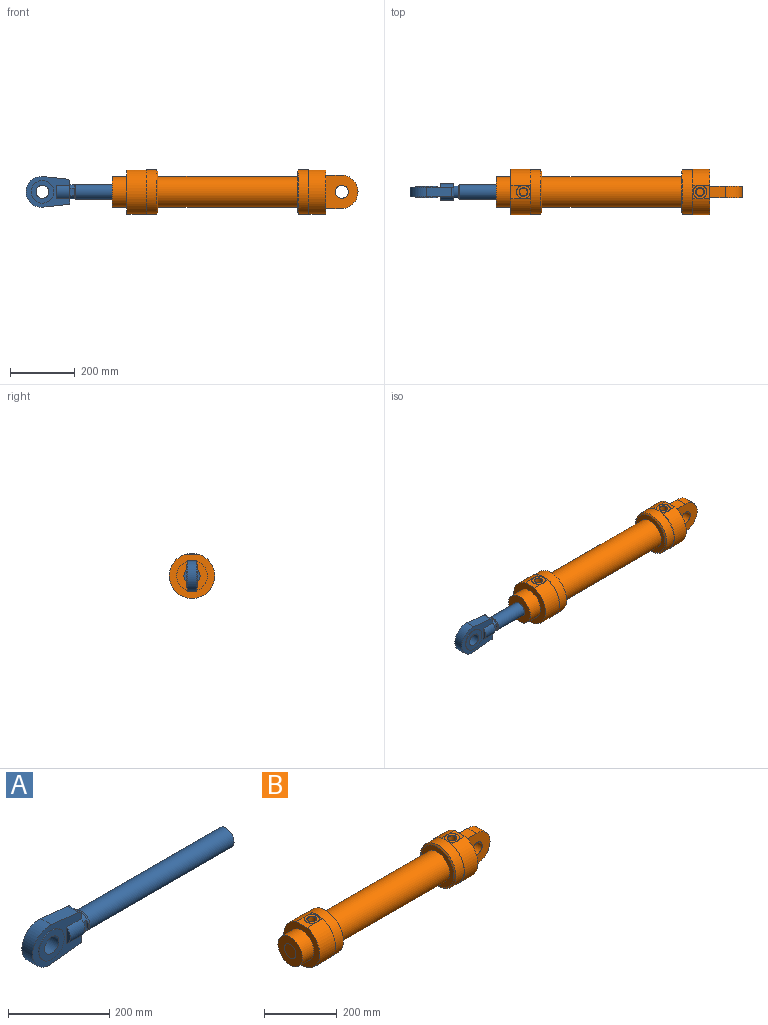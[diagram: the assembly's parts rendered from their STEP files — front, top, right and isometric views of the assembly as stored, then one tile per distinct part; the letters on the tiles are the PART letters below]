
ASSEMBLY  parts=2 mates=1
PART A: 45 faces, bbox 556x50x95 mm
  f0: cylinder r=20mm len=40mm, axis (0,-1,0), area 4398.2mm2, adj f1,f2
  f1: plane 70x70mm, normal (0,1,0), area 2591.8mm2, adj f0,f3
  f2: plane 70x70mm, normal (0,-1,0), area 2591.8mm2, adj f0,f5
  f3: cylinder r=35mm len=70mm, axis (0,-1,0), area 549.8mm2, adj f1,f12
  f4: plane 40x10mm, normal (-1,0,0), area 279.6mm2, adj f11,f12
  f5: cylinder r=35mm len=70mm, axis (0,-1,0), area 549.8mm2, adj f2,f15
  f6: plane 40x10mm, normal (-1,0,0), area 279.6mm2, adj f14,f15
  f7: plane 79.97x30mm, normal (0.1,0,-0.99), area 2412.3mm2, adj f8,f12,f13,f15
  f8: cylinder r=47.5mm len=95mm, axis (0,-1,0), area 4773.9mm2, adj f7,f9,f12,f15
  f9: plane 75.49x30mm, normal (0.1,0,0.99), area 2277.2mm2, adj f8,f10,f12,f15
  f10: cylinder r=9mm len=30mm, axis (0,-1,0), area 396mm2, adj f9,f12,f15,f16
  f11: cylinder r=25mm len=41mm, axis (1,0,0), area 1901mm2, adj f4,f12,f16
  f12: plane 136x95mm, normal (0,1,0), area 5672.5mm2, adj f3,f4,f7,f8,f9,f10,f11,f13
  f13: cylinder r=4mm len=30mm, axis (0,-1,0), area 176mm2, adj f7,f12,f15,f16
  f14: cylinder r=25mm len=41mm, axis (1,0,0), area 1901mm2, adj f6,f15,f16
  f15: plane 136x95mm, normal (0,-1,0), area 5672.5mm2, adj f5,f6,f7,f8,f9,f10,f13,f14
  f16: plane 65.29x50mm, normal (1,0,0), area 1178.1mm2, adj f10,f11,f12,f13,f14,f15,f17,f18
  f17: cone r=21.49mm half-angle=45deg, axis (1,0,0), area 0.6mm2, adj f16,f18,f19,f22
  f18: plane 23.52x13mm, normal (0,-1,0), area 305.7mm2, adj f16,f17,f20,f21,f22,f24
  f19: plane 23.52x13mm, normal (0,1,0), area 305.7mm2, adj f16,f17,f20,f22,f23,f24
  f20: cone r=21.49mm half-angle=45deg, axis (1,0,0), area 0.6mm2, adj f16,f18,f19,f24
  f21: plane 23.52x3.5mm, normal (-1,0,0), area 55.8mm2, adj f18,f25
  f22: cylinder r=21.5mm len=36mm, axis (1,0,0), area 554.2mm2, adj f17,f18,f19,f25
  f23: plane 23.52x3.5mm, normal (-1,0,0), area 55.8mm2, adj f19,f25
  f24: cylinder r=21.5mm len=36mm, axis (1,0,0), area 554.2mm2, adj f18,f19,f20,f25
  f25: cone r=22mm half-angle=15deg, axis (1,0,0), area 534.1mm2, adj f21,f22,f23,f24,f26
  f26: cylinder r=22.5mm len=403.27mm, axis (1,0,0), area 57010.7mm2, adj f25,f27
  f27: plane 45x45mm, normal (1,0,0), area 1590.4mm2, adj f26
  f28: plane 65x65mm, normal (0,1,0), area 299.2mm2, adj f30,f31
  f29: plane 65x65mm, normal (0,-1,0), area 299.2mm2, adj f30,f31
  f30: cylinder r=32.5mm len=65mm, axis (0,-1,0), area 439mm2, adj f28,f29
  f31: cylinder r=31mm len=62mm, axis (0,-1,0), area 418.8mm2, adj f28,f29
  f32: cylinder r=32.5mm len=65mm, axis (0,-1,0), area 439mm2, adj f33,f34
  f33: plane 65x65mm, normal (0,-1,0), area 299.2mm2, adj f32,f35
  f34: plane 65x65mm, normal (0,1,0), area 299.2mm2, adj f32,f35
  f35: cylinder r=31mm len=62mm, axis (0,-1,0), area 418.8mm2, adj f33,f34
  f36: plane 33.16x33.16mm, normal (1,0,0), area 23.8mm2, adj f38,f40
  f37: plane 33.38x33.38mm, normal (-1,0,0), area 35.1mm2, adj f39,f40
  f38: cone r=16.58mm half-angle=45deg, axis (-1,0,0), area 16mm2, adj f36,f39
  f39: cylinder r=16.69mm len=33.38mm, axis (-1,0,0), area 346.9mm2, adj f37,f38
  f40: cylinder r=16.35mm len=32.7mm, axis (1,0,0), area 328.7mm2, adj f36,f37
  f41: plane 33.16x33.16mm, normal (-1,0,0), area 863.6mm2, adj f42
  f42: cone r=16.58mm half-angle=45deg, axis (1,0,0), area 16mm2, adj f41,f44
  f43: plane 33.38x33.38mm, normal (1,0,0), area 874.9mm2, adj f44
  f44: cylinder r=16.69mm len=33.38mm, axis (-1,0,0), area 116.2mm2, adj f42,f43
PART B: 46 faces, bbox 760x140x139 mm
  f0: cylinder r=70mm len=140mm, axis (1,0,0), area 20723.4mm2, adj f1,f14,f21,f29,f34
  f1: cylinder r=21mm len=42mm, axis (0,0,-1), area 62.7mm2, adj f0,f21,f29,f36
  f2: cylinder r=12.12mm len=24.25mm, axis (0,0,-1), area 1502.7mm2, adj f5,f26
  f3: plane 104x100mm, normal (0,1,0), area 7982.8mm2, adj f14,f17,f18,f28,f32
  f4: cone r=13.4mm half-angle=45deg, axis (0,0,1), area 144.6mm2, adj f22,f36
  f5: plane 24.25x24.25mm, normal (0,0,1), area 461.9mm2, adj f2
  f6: cylinder r=47.5mm len=432mm, axis (1,0,0), area 128931mm2, adj f11,f15
  f7: cylinder r=21mm len=42mm, axis (0,0,-1), area 63.1mm2, adj f25,f27,f30,f31
  f8: plane 140x137mm, normal (-1,0,0), area 8224.1mm2, adj f27,f31,f35
  f9: cylinder r=69mm len=138mm, axis (-1,0,0), area 13922.4mm2, adj f10,f24,f34
  f10: cone r=64mm half-angle=60deg, axis (1,0,0), area 2412.4mm2, adj f9,f11
  f11: plane 128x128mm, normal (-1,0,0), area 5779.7mm2, adj f6,f10
  f12: plane 95x95mm, normal (-1,0,0), area 5497.8mm2, adj f35,f37
  f13: plane 32.99x2mm, normal (-1,0,0), area 44.1mm2, adj f23,f30
  f14: plane 140x137mm, normal (1,0,0), area 11672.4mm2, adj f0,f3,f18,f19,f21,f28
  f15: plane 128x128mm, normal (1,0,0), area 5779.7mm2, adj f6,f33
  f16: plane 140x137mm, normal (1,0,0), area 399.3mm2, adj f23,f30,f31
  f17: cylinder r=20mm len=40mm, axis (0,-1,0), area 4398.2mm2, adj f3,f19
  f18: plane 48x35mm, normal (0,0,1), area 1680mm2, adj f3,f14,f19,f32
  f19: plane 104x100mm, normal (0,-1,0), area 7982.8mm2, adj f14,f17,f18,f28,f32
  f20: plane 24.25x24.25mm, normal (0,0,1), area 461.9mm2, adj f22
  f21: plane 40.55x24.52mm, normal (0,0,1), area 529mm2, adj f0,f1,f14
  f22: cylinder r=12.12mm len=24.25mm, axis (0,0,-1), area 1502.7mm2, adj f4,f20
  f23: cylinder r=69mm len=138mm, axis (1,0,0), area 13922.4mm2, adj f13,f16,f33
  f24: plane 32.99x2mm, normal (1,0,0), area 44.1mm2, adj f9,f29
  f25: plane 42x42mm, normal (0,0,1), area 821.3mm2, adj f7,f26
  f26: cone r=13.4mm half-angle=45deg, axis (0,0,1), area 144.6mm2, adj f2,f25
  f27: plane 40.55x33.52mm, normal (0,0,1), area 893.9mm2, adj f7,f8,f31
  f28: plane 48x35mm, normal (0,0,-1), area 1680mm2, adj f3,f14,f19,f32
  f29: plane 40.55x16.52mm, normal (0,0,1), area 204.6mm2, adj f0,f1,f24,f34
  f30: plane 40.55x16.52mm, normal (0,0,1), area 204.6mm2, adj f7,f13,f16,f31
  f31: cylinder r=70mm len=140mm, axis (1,0,0), area 24310.2mm2, adj f7,f8,f16,f27,f30
  f32: cylinder r=52mm len=104mm, axis (0,1,0), area 5717.7mm2, adj f3,f18,f19,f28
  f33: cone r=64mm half-angle=60deg, axis (-1,0,0), area 2412.4mm2, adj f15,f23
  f34: plane 140x137mm, normal (-1,0,0), area 399.3mm2, adj f0,f9,f29
  f35: cylinder r=47.5mm len=95mm, axis (1,0,0), area 13430.3mm2, adj f8,f12
  f36: plane 42x42mm, normal (0,0,1), area 821.3mm2, adj f1,f4
  f37: plane 45x45mm, normal (-1,0,0), area 1590.4mm2, adj f12
  f38: plane 63.5x63.5mm, normal (0,1,0), area 147.9mm2, adj f39,f41
  f39: cylinder r=31.75mm len=63.5mm, axis (0,-1,0), area 319.2mm2, adj f38,f40
  f40: plane 63.5x63.5mm, normal (0,-1,0), area 147.9mm2, adj f39,f41
  f41: cylinder r=31mm len=62mm, axis (0,-1,0), area 311.6mm2, adj f38,f40
  f42: plane 63.5x63.5mm, normal (0,-1,0), area 147.9mm2, adj f44,f45
  f43: plane 63.5x63.5mm, normal (0,1,0), area 147.9mm2, adj f44,f45
  f44: cylinder r=31mm len=62mm, axis (0,-1,0), area 311.6mm2, adj f42,f43
  f45: cylinder r=31.75mm len=63.5mm, axis (0,-1,0), area 319.2mm2, adj f42,f43
PLACE A t=(-110.91,0,0)mm
PLACE B at identity fixed
MATE slider A.f11 <-> B.f0  axis (1,0,0) through (183.09,0,0)mm
